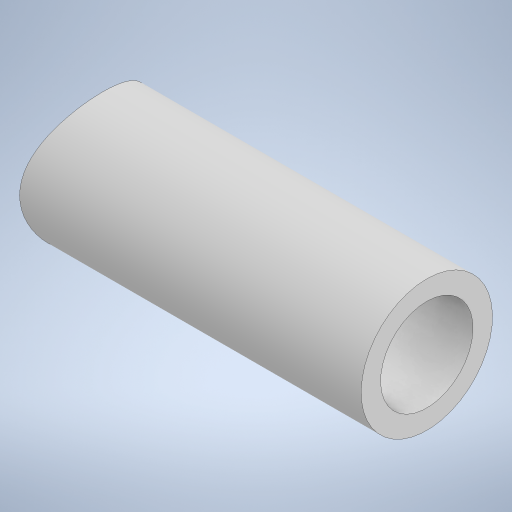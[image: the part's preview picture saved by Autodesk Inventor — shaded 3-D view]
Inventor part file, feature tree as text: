
AUTODESK INVENTOR PART (.ipt)
format: ipt  version: 2023 (Build 270158000, 158)  size: 225,792 bytes
history: native  units: in
note: dims shown in document units (in); Inventor stores cm internally (conversion verified against a paired STEP export)
features: extrude x2, sketch x2
ambient origin geometry x8: Origin, YZ Plane, XZ Plane, XY Plane, X Axis, Y Axis, Z Axis, Center Point
bodies: Solid1 (feature_tree)
feature tree (4):
  extrude  "Extrusion1"  Depth=0.0938in
  extrude  "Extrusion2"  Depth=0.25in
  sketch  "Sketch1"  dims[d0=0.0938in d1=0.066in]
  sketch  "Sketch2"  dims[d2=0.25in d3=0.0in d4=0.1875in d5=0.075in d6=0.25in d7=0.0in]
